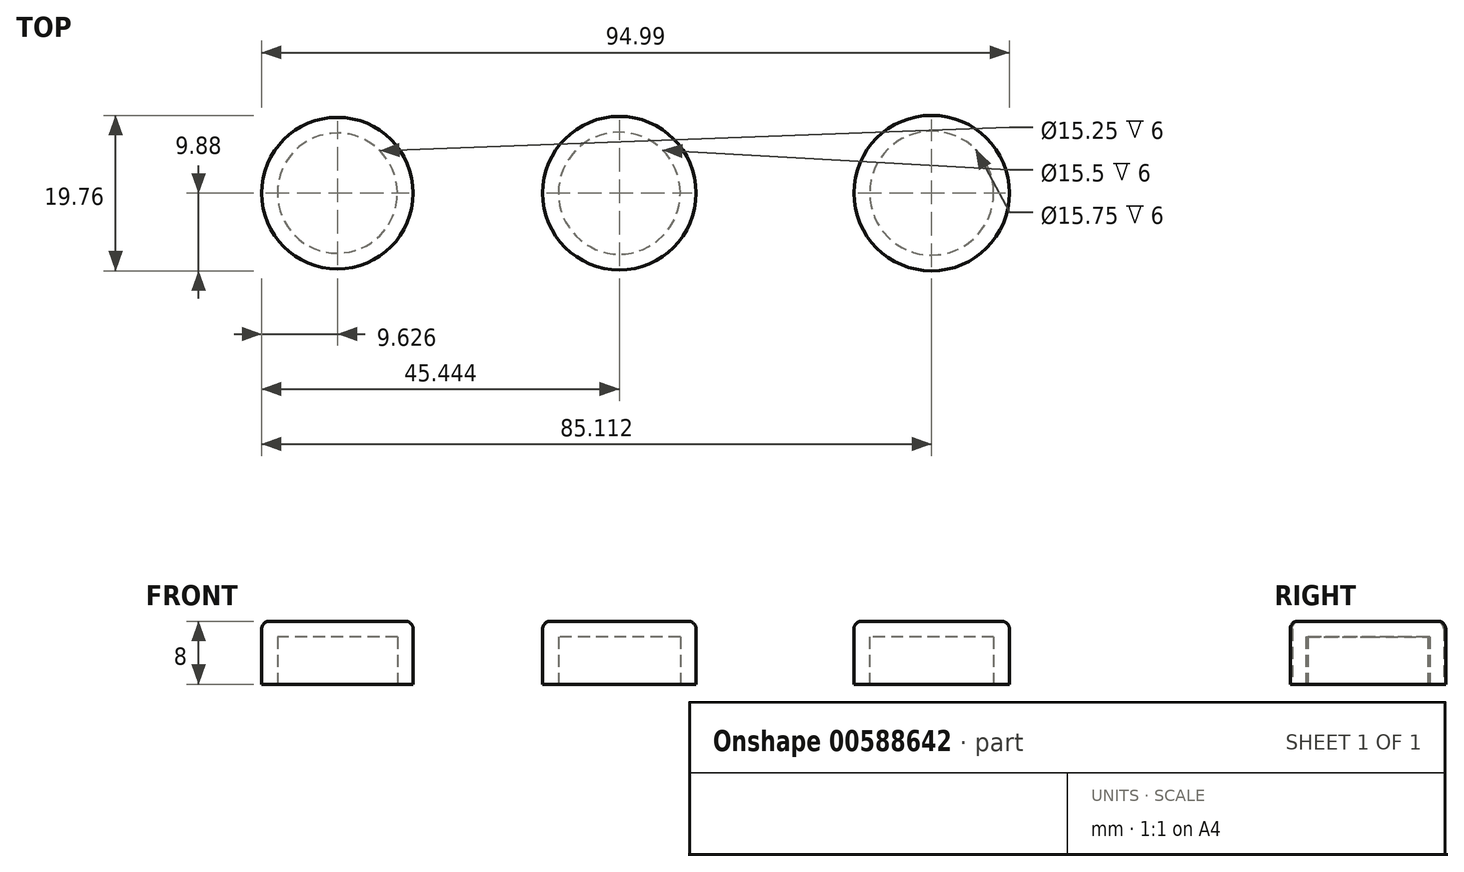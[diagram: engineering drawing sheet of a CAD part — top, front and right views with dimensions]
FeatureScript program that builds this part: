
annotation { "Feature Type Name" : "Feature", "Feature Type Description" : "" }
export const myFeature = defineFeature(function(context is Context, id is Id, definition is map)
    precondition{}
    {
        {
            var Q0;
            Q0=qCreatedBy(makeId("Top.planeOp"),FACE);
            var sketch = newSketch(context, id + "F0", { "sketchPlane" : qUnion([Q0])});
            skCircle(sketch, "E0", {"center": v(-31.63, 0) * mm, "radius": 7.62 * mm});
            skCircle(sketch, "E1", {"center": v(4.18, 0) * mm, "radius": 7.75 * mm});
            skCircle(sketch, "E2", {"center": v(43.85, 0) * mm, "radius": 7.88 * mm});
            skCircle(sketch, "E3", {"center": v(-31.63, 0) * mm, "radius": 9.62 * mm});
            skCircle(sketch, "E4", {"center": v(4.18, 0) * mm, "radius": 9.75 * mm});
            skCircle(sketch, "E5", {"center": v(43.85, 0) * mm, "radius": 9.88 * mm});
            skSolve(sketch);
        }
        {
            var Q0;
            Q0 = qSketchRegion(id + "F0", true);
            extrude(context, id + "F1", {"entities" : qUnion([Q0]), "depth" : 6 * mm, "offsetDistance" : 25 * mm});
        }
        {
            var Q0;
            Q0=makeQuery(id+"F1.opExtrude","CAP_FACE",FACE,{"disambiguationData":[OSD([sQuery(id+"F0.wireOp",EDGE,"E1"),sQuery(id+"F0.wireOp",EDGE,"E4")])],"isStart":false});
            var sketch = newSketch(context, id + "F2", { "sketchPlane" : qUnion([Q0])});
            skCircle(sketch, "E6.0", {"center": v(-31.63, 0) * mm, "radius": 9.62 * mm});
            skCircle(sketch, "E6.1", {"center": v(4.18, 0) * mm, "radius": 9.75 * mm});
            skCircle(sketch, "E6.2", {"center": v(43.85, 0) * mm, "radius": 9.88 * mm});
            skSolve(sketch);
        }
        {
            var Q0;
            Q0 = qSketchRegion(id + "F2", true);
            extrude(context, id + "F3", {"entities" : qUnion([Q0]), "operationType" : NewBodyOperationType.ADD, "depth" : 2 * mm, "offsetDistance" : 25 * mm});
        }
        {
            var Q0;
            Q0=makeQuery(id+"F3.opExtrude","CAP_EDGE",EDGE,{"disambiguationData":[OSD([sQuery(id+"F2.wireOp",EDGE,"E6.0")])],"isStart":false});
            var Q1;
            Q1=makeQuery(id+"F3.opExtrude","CAP_EDGE",EDGE,{"disambiguationData":[OSD([sQuery(id+"F2.wireOp",EDGE,"E6.1")])],"isStart":false});
            var Q2;
            Q2=makeQuery(id+"F3.opExtrude","CAP_EDGE",EDGE,{"disambiguationData":[OSD([sQuery(id+"F2.wireOp",EDGE,"E6.2")])],"isStart":false});
            fillet(context, id + "F4", {"entities" : qUnion([Q0, Q1, Q2]), "radius" : 1 * mm, "tangentPropagation" : true, "allowEdgeOverflow" : false});
        }
    });
